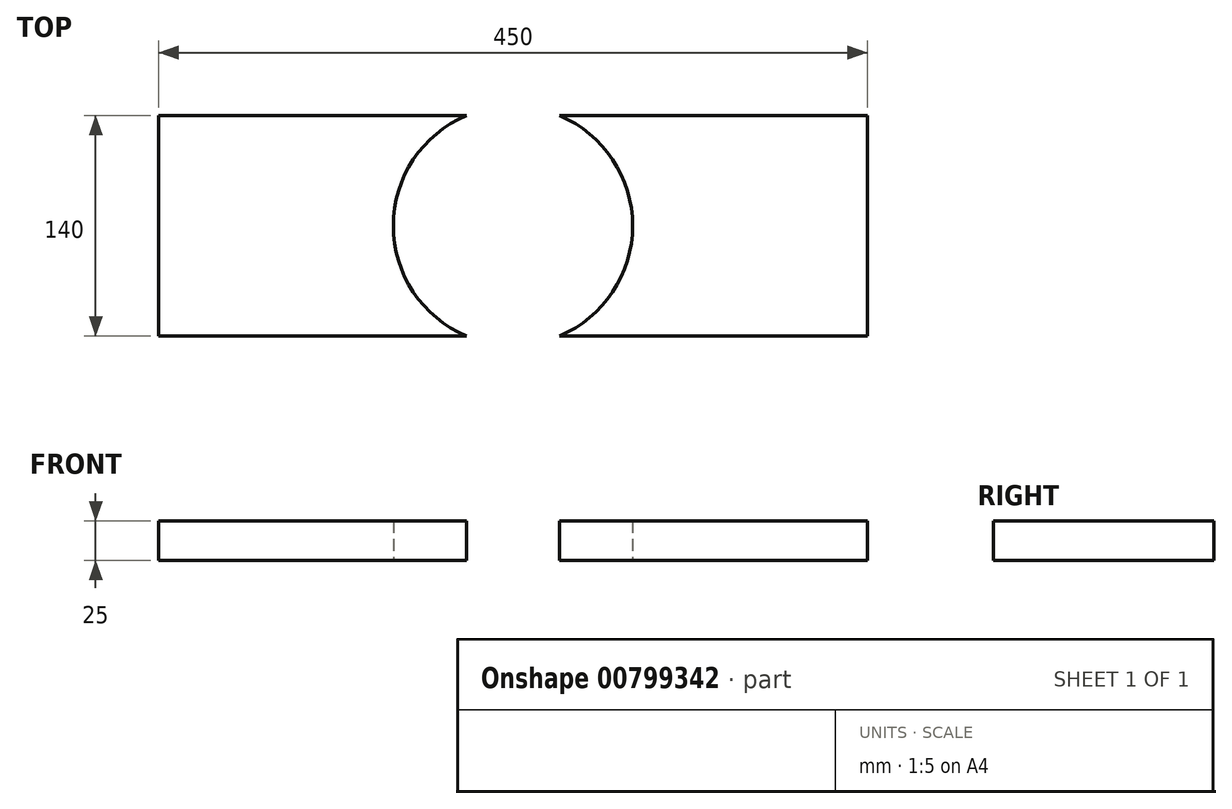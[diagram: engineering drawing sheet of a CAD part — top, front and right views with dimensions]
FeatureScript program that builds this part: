
annotation { "Feature Type Name" : "Feature", "Feature Type Description" : "" }
export const myFeature = defineFeature(function(context is Context, id is Id, definition is map)
    precondition{}
    {
        {
            var Q0;
            Q0=qCreatedBy(makeId("Top.planeOp"),FACE);
            var sketch = newSketch(context, id + "F0", { "sketchPlane" : qUnion([Q0])});
            skCircle(sketch, "E0", {"center": v(0, 0) * mm, "radius": 76 * mm});
            skCircle(sketch, "E1", {"center": v(0, 0) * mm, "radius": 64.5 * mm});
            skLineSegment(sketch, "E2.bottom", {"start": v(225, 70) * mm, "end": v(-225, 70) * mm});
            skLineSegment(sketch, "E2.top", {"start": v(225, -70) * mm, "end": v(-225, -70) * mm});
            skLineSegment(sketch, "E2.left", {"start": v(225, 70) * mm, "end": v(225, -70) * mm});
            skLineSegment(sketch, "E2.right", {"start": v(-225, 70) * mm, "end": v(-225, -70) * mm});
            skLineSegment(sketch, "E3.bottom", {"start": v(-195, -45) * mm, "end": v(-105, -45) * mm, "construction": true});
            skLineSegment(sketch, "E3.top", {"start": v(-195, 45) * mm, "end": v(-105, 45) * mm, "construction": true});
            skLineSegment(sketch, "E3.left", {"start": v(-195, -45) * mm, "end": v(-195, 45) * mm, "construction": true});
            skLineSegment(sketch, "E3.right", {"start": v(-105, -45) * mm, "end": v(-105, 45) * mm, "construction": true});
            skPoint(sketch, "E3.middle", {"position": v(-150, 0) * mm});
            skLineSegment(sketch, "E4.bottom", {"start": v(105, -45) * mm, "end": v(195, -45) * mm, "construction": true});
            skLineSegment(sketch, "E4.top", {"start": v(105, 45) * mm, "end": v(195, 45) * mm, "construction": true});
            skLineSegment(sketch, "E4.left", {"start": v(105, -45) * mm, "end": v(105, 45) * mm, "construction": true});
            skLineSegment(sketch, "E4.right", {"start": v(195, -45) * mm, "end": v(195, 45) * mm, "construction": true});
            skPoint(sketch, "E4.middle", {"position": v(150, 0) * mm});
            skSolve(sketch);
        }
        {
            var Q0;
            {var subQ5=sQuery(id+"F0.wireOp",EDGE,"E2.left");Q0=makeQuery(id+"F0.imprint","IMPRINT",FACE,{"disambiguationData":[TD([[makeQuery(id+"F0.imprint","IMPRINT",EDGE,{"derivedFrom":subQ5}),-1.0]])]});}
            var Q1;
            {var subQ5=sQuery(id+"F0.wireOp",EDGE,"E2.right");Q1=makeQuery(id+"F0.imprint","IMPRINT",FACE,{"disambiguationData":[TD([[makeQuery(id+"F0.imprint","IMPRINT",EDGE,{"derivedFrom":subQ5}),1.0]])]});}
            extrude(context, id + "F1", {"entities" : qUnion([Q0, Q1]), "depth" : 25 * mm, "offsetDistance" : 25 * mm});
        }
    });
